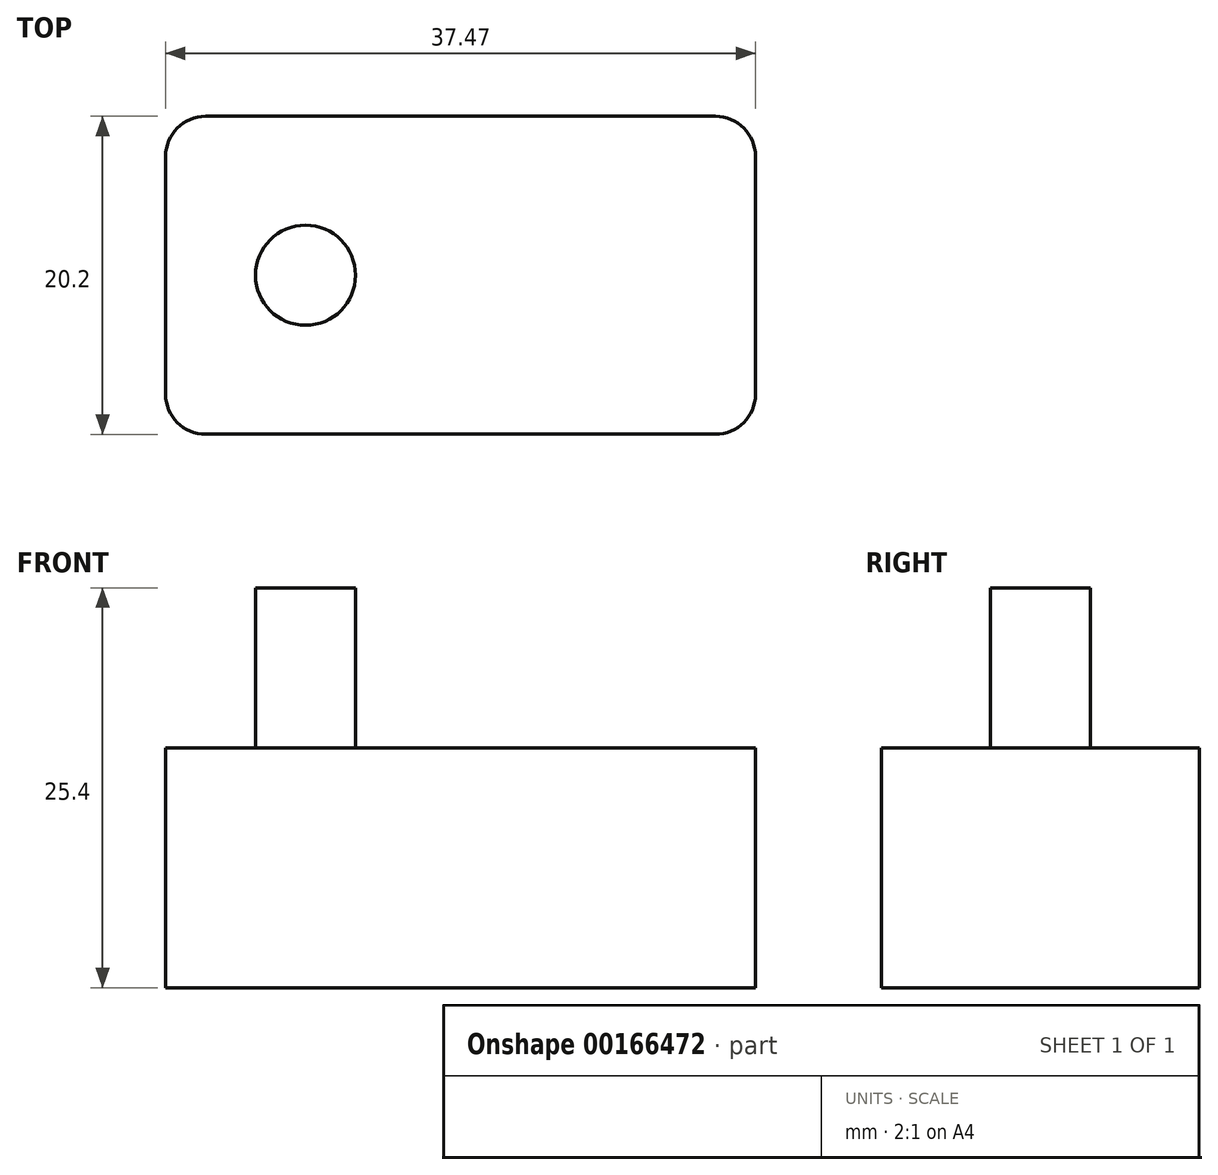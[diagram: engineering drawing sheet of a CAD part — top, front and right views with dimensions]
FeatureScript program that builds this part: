
annotation { "Feature Type Name" : "Feature", "Feature Type Description" : "" }
export const myFeature = defineFeature(function(context is Context, id is Id, definition is map)
    precondition{}
    {
        {
            var Q0;
            Q0=qCreatedBy(makeId("Top.planeOp"),FACE);
            var sketch = newSketch(context, id + "F0", { "sketchPlane" : qUnion([Q0])});
            skLineSegment(sketch, "E0.bottom", {"start": v(-31.3, 3.3) * mm, "end": v(6.16, 3.3) * mm});
            skLineSegment(sketch, "E0.top", {"start": v(-31.3, -16.89) * mm, "end": v(6.16, -16.89) * mm});
            skLineSegment(sketch, "E0.left", {"start": v(-31.3, 3.3) * mm, "end": v(-31.3, -16.89) * mm});
            skLineSegment(sketch, "E0.right", {"start": v(6.16, 3.3) * mm, "end": v(6.16, -16.89) * mm});
            skSolve(sketch);
        }
        {
            var Q0;
            Q0 = qSketchRegion(id + "F0", true);
            extrude(context, id + "F1", {"entities" : qUnion([Q0]), "depth" : 25.4 * mm});
        }
        {
            var Q0;
            Q0=makeQuery(id+"F1.opExtrude","CAP_FACE",FACE,{"disambiguationData":[OSD([sQuery(id+"F0.wireOp",EDGE,"E0.bottom"),sQuery(id+"F0.wireOp",EDGE,"E0.top"),sQuery(id+"F0.wireOp",EDGE,"E0.left"),sQuery(id+"F0.wireOp",EDGE,"E0.right")])],"isStart":false});
            var sketch = newSketch(context, id + "F2", { "sketchPlane" : qUnion([Q0])});
            skLineSegment(sketch, "E1", {"start": v(-31.3, -6.8) * mm, "end": v(6.16, -6.8) * mm});
            skPoint(sketch, "E2", {"position": v(-2.73, -6.8) * mm});
            skPoint(sketch, "E3", {"position": v(-22.42, -6.8) * mm});
            skCircle(sketch, "E4", {"center": v(-22.42, -6.8) * mm, "radius": 3.18 * mm});
            skCircle(sketch, "E5", {"center": v(-2.73, -6.8) * mm, "radius": 3.18 * mm});
            skSolve(sketch);
        }
        {
            var Q0;
            {var subQ0=sQuery(id+"F2.wireOp",EDGE,"E4");var subQ1=sQuery(id+"F2.wireOp",EDGE,"E1");var subQ2=makeQuery(id+"F2.imprint","INTERSECT",VERTEX,{"disambiguationData":[OD(0.0)],"derivedFrom":[subQ1,subQ0]});Q0=makeQuery(id+"F2.imprint","IMPRINT",FACE,{"disambiguationData":[TD([[makeQuery(id+"F2.imprint","IMPRINT",EDGE,{"disambiguationData":[TD([[subQ2,-1.0]])],"derivedFrom":subQ1}),-1.0]])]});}
            var Q1;
            {var subQ0=sQuery(id+"F2.wireOp",EDGE,"E4");var subQ1=sQuery(id+"F2.wireOp",EDGE,"E1");var subQ2=makeQuery(id+"F2.imprint","INTERSECT",VERTEX,{"disambiguationData":[OD(0.0)],"derivedFrom":[subQ1,subQ0]});Q1=makeQuery(id+"F2.imprint","IMPRINT",FACE,{"disambiguationData":[TD([[makeQuery(id+"F2.imprint","IMPRINT",EDGE,{"disambiguationData":[TD([[subQ2,-1.0]])],"derivedFrom":subQ1}),1.0]])]});}
            var Q2;
            {var subQ0=sQuery(id+"F2.wireOp",EDGE,"E5");var subQ1=sQuery(id+"F2.wireOp",EDGE,"E1");var subQ2=makeQuery(id+"F2.imprint","INTERSECT",VERTEX,{"disambiguationData":[OD(0.0)],"derivedFrom":[subQ1,subQ0]});Q2=makeQuery(id+"F2.imprint","IMPRINT",FACE,{"disambiguationData":[TD([[makeQuery(id+"F2.imprint","IMPRINT",EDGE,{"disambiguationData":[TD([[subQ2,-1.0]])],"derivedFrom":subQ1}),1.0]])]});}
            var Q3;
            {var subQ0=sQuery(id+"F2.wireOp",EDGE,"E5");var subQ1=sQuery(id+"F2.wireOp",EDGE,"E1");var subQ2=makeQuery(id+"F2.imprint","INTERSECT",VERTEX,{"disambiguationData":[OD(0.0)],"derivedFrom":[subQ1,subQ0]});Q3=makeQuery(id+"F2.imprint","IMPRINT",FACE,{"disambiguationData":[TD([[makeQuery(id+"F2.imprint","IMPRINT",EDGE,{"disambiguationData":[TD([[subQ2,-1.0]])],"derivedFrom":subQ1}),-1.0]])]});}
            extrude(context, id + "F3", {"entities" : qUnion([Q0, Q1, Q2, Q3]), "operationType" : NewBodyOperationType.REMOVE, "oppositeDirection" : true, "depth" : 10.16 * mm});
        }
        {
            var Q0;
            Q0=makeQuery(id+"F1.opExtrude","SWEPT_EDGE",EDGE,{"disambiguationData":[OSD([sQuery(id+"F0.wireOp",EDGE,"E0.top"),sQuery(id+"F0.wireOp",EDGE,"E0.left")])]});
            var Q1;
            Q1=makeQuery(id+"F1.opExtrude","SWEPT_EDGE",EDGE,{"disambiguationData":[OSD([sQuery(id+"F0.wireOp",EDGE,"E0.top"),sQuery(id+"F0.wireOp",EDGE,"E0.right")])]});
            var Q2;
            Q2=makeQuery(id+"F1.opExtrude","SWEPT_EDGE",EDGE,{"disambiguationData":[OSD([sQuery(id+"F0.wireOp",EDGE,"E0.bottom"),sQuery(id+"F0.wireOp",EDGE,"E0.right")])]});
            var Q3;
            Q3=makeQuery(id+"F1.opExtrude","SWEPT_EDGE",EDGE,{"disambiguationData":[OSD([sQuery(id+"F0.wireOp",EDGE,"E0.bottom"),sQuery(id+"F0.wireOp",EDGE,"E0.left")])]});
            fillet(context, id + "F4", {"entities" : qUnion([Q0, Q1, Q2, Q3]), "radius" : 2.54 * mm, "tangentPropagation" : true, "allowEdgeOverflow" : false});
        }
    });
